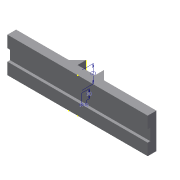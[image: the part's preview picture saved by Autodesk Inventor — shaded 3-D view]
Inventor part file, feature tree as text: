
AUTODESK INVENTOR PART (.ipt)
format: ipt  version: 2015 (Build 190159000, 159)  size: 116,736 bytes
history: native  units: mm
features: sketch x11, extrude x3, split x2
ambient origin geometry x8: Origin, YZ Plane, XZ Plane, XY Plane, X Axis, Y Axis, Z Axis, Center Point
bodies: Solid1 (feature_tree)
feature tree (16):
  extrude  "Extrusion1"  Depth=1.0mm
  extrude  "Extrusion2"  Depth=4.0mm TaperAngle=0.0deg
  extrude  "Extrusion3"  Depth=0.5mm
  split  "Split1"
  sketch  "Sketch5"  dims[d19=0.5mm]
  sketch  "Sketch6"  dims[d20=2.0mm d21=0.0mm]
  sketch  "Sketch7"  dims[d22=1.3333mm]
  sketch  "Sketch8"  dims[d23=1.3333mm]
  sketch  "Sketch9"  dims[d24=0.3mm]
  sketch  "Sketch10"  dims[d25=1.0mm]
  split  "Split2"
  sketch  "Sketch1"  dims[d7=2.0mm d8=1.0mm]
  sketch  "Sketch2"  dims[d9=2.0mm d10=4.0mm d11=0.0mm]
  sketch  "Sketch3"  dims[d14=0.5mm d15=0.5mm]
  sketch  "Sketch4"  dims[d16=2.0mm d17=0.0mm]
  sketch  "Sketch11"  dims[d26=2.0mm d27=0.5mm d29=8.0mm d30=8.0mm d31=1.3333mm d32=1.3333mm d33=0.3mm]
